# Revit family: okamura_CDC6BK_Cynara_Black Body Without Armrest Hollow Caster
name_source: partatom
category: Furniture
revit_build: Autodesk Revit 2017 (Build: 20160225_1515(x64)
units: mm (PartAtom-declared; Revit-internal decimal feet)

## family parameters
Always vertical = Yes
Cut with Voids When Loaded = No
OmniClass Number = 23.40.20.00
OmniClass Title = General Furniture and Specialties
Room Calculation Point = No
Shared = No
Work Plane-Based = No

## types (6) — shared parameters
Assembly Code = E2020200
Body & Base = okm_G721
Caster = okm_gray GR4
D = 505 mm
Gas Lift = okm_silver FX4
H = 999 mm
Keynote = 12490
Kind = Chair
Manufacturer = Okamura Corporation
Other = okm_G155
Product Categories = Office Seating
Product Number = CDC6BK
URL = http://www.okamura.co.jp
W = 492 mm

## per-type parameters (varying)
| type | Mesh |
| F2X1(Black) | okm_F2X1 |
| F2X2(White) | okm_F2X2 |
| F2X3(Dark Gray) | okm_F2X3 |
| F2X4(Sage) | okm_F2X4 |
| F2X5(Dark Green) | okm_F2X5 |
| F2X6(Orange Red) | okm_F2X6 |
